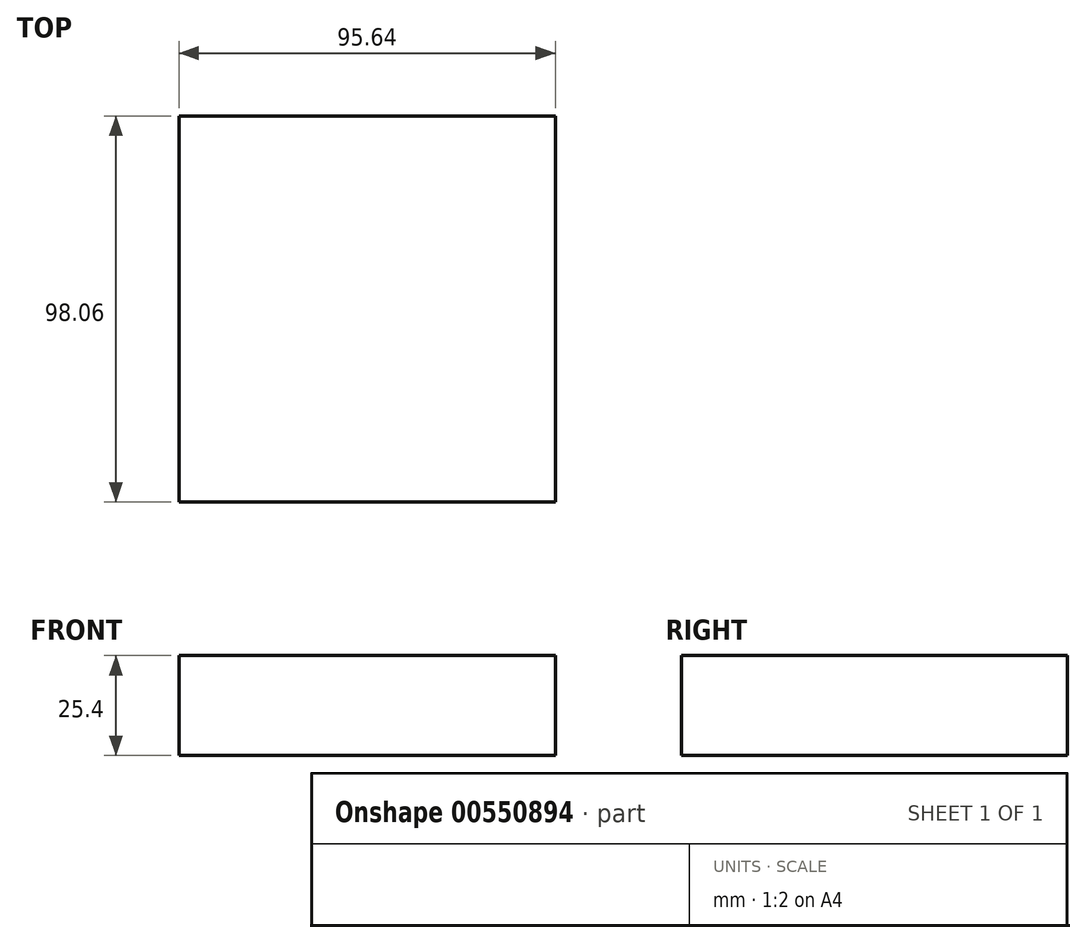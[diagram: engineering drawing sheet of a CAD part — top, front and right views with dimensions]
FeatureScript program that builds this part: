
annotation { "Feature Type Name" : "Feature", "Feature Type Description" : "" }
export const myFeature = defineFeature(function(context is Context, id is Id, definition is map)
    precondition{}
    {
        {
            var Q0;
            Q0=qCreatedBy(makeId("Top.planeOp"),FACE);
            var sketch = newSketch(context, id + "F0", { "sketchPlane" : qUnion([Q0])});
            skLineSegment(sketch, "E0.bottom", {"start": v(47.82, 49.03) * mm, "end": v(-47.82, 49.03) * mm});
            skLineSegment(sketch, "E0.top", {"start": v(47.82, -49.03) * mm, "end": v(-47.82, -49.03) * mm});
            skLineSegment(sketch, "E0.left", {"start": v(47.82, 49.03) * mm, "end": v(47.82, -49.03) * mm});
            skLineSegment(sketch, "E0.right", {"start": v(-47.82, 49.03) * mm, "end": v(-47.82, -49.03) * mm});
            skPoint(sketch, "E0.middle", {"position": v(0, 0) * mm});
            skSolve(sketch);
        }
        {
            var Q0;
            Q0 = qSketchRegion(id + "F0", true);
            extrude(context, id + "F1", {"entities" : qUnion([Q0]), "depth" : 25.4 * mm, "offsetDistance" : 25.4 * mm});
        }
    });
